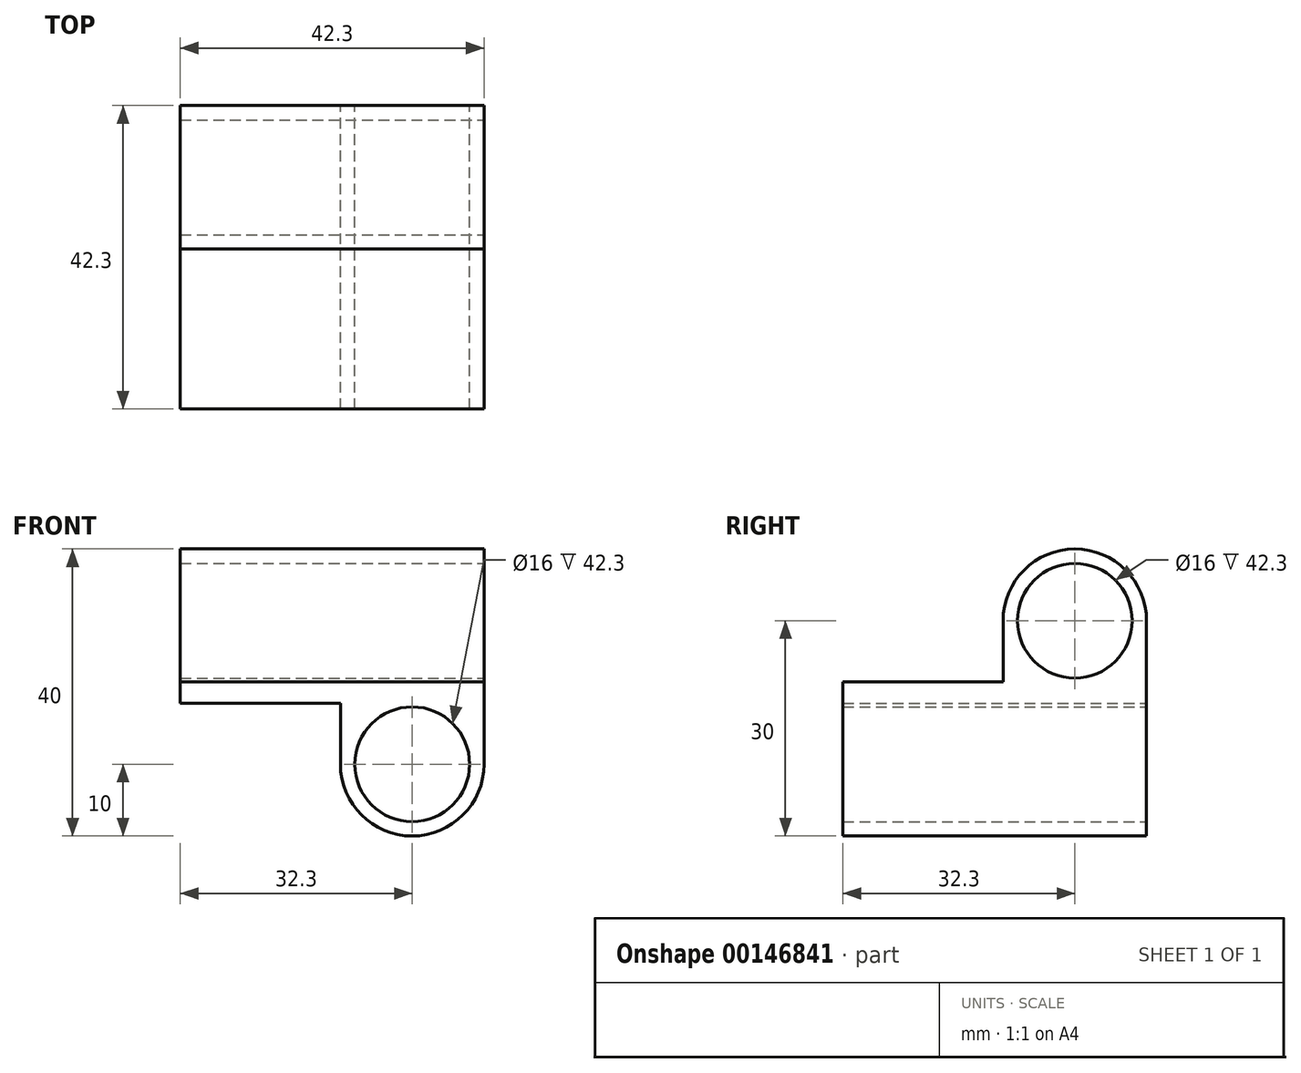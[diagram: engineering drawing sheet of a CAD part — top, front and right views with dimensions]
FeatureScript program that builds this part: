
annotation { "Feature Type Name" : "Feature", "Feature Type Description" : "" }
export const myFeature = defineFeature(function(context is Context, id is Id, definition is map)
    precondition{}
    {
        {
            var Q0;
            Q0=qCreatedBy(makeId("Front.planeOp"),FACE);
            var sketch = newSketch(context, id + "F0", { "sketchPlane" : qUnion([Q0])});
            skPoint(sketch, "E0.middle", {"position": v(0, 0) * mm});
            skCircle(sketch, "E1", {"center": v(-10, -10) * mm, "radius": 10 * mm});
            skCircle(sketch, "E2", {"center": v(-10, -10) * mm, "radius": 8 * mm});
            skLineSegment(sketch, "E3.bottom", {"start": v(0, 0) * mm, "end": v(-20, 0) * mm});
            skLineSegment(sketch, "E3.top", {"start": v(0, -10) * mm, "end": v(-20, -10) * mm});
            skLineSegment(sketch, "E3.left", {"start": v(0, 0) * mm, "end": v(0, -10) * mm});
            skLineSegment(sketch, "E3.right", {"start": v(-20, 0) * mm, "end": v(-20, -10) * mm});
            skLineSegment(sketch, "E4.bottom", {"start": v(-42.3, 0) * mm, "end": v(-20, 0) * mm});
            skLineSegment(sketch, "E4.top", {"start": v(-42.3, -1.5) * mm, "end": v(-20, -1.5) * mm});
            skLineSegment(sketch, "E4.left", {"start": v(-42.3, 0) * mm, "end": v(-42.3, -1.5) * mm});
            skLineSegment(sketch, "E4.right", {"start": v(-20, 0) * mm, "end": v(-20, -1.5) * mm});
            skSolve(sketch);
        }
        {
            var Q0;
            Q0=qSketchRegion(id+"F0",true);
            extrude(context, id + "F1", {"entities" : qUnion([Q0]), "depth" : 42.3 * mm});
        }
        {
            var Q0;
            Q0=qCreatedBy(makeId("Right.planeOp"),FACE);
            var sketch = newSketch(context, id + "F2", { "sketchPlane" : qUnion([Q0])});
            skCircle(sketch, "E5", {"center": v(-10, 10) * mm, "radius": 8 * mm});
            skCircle(sketch, "E6", {"center": v(-10, 10) * mm, "radius": 10 * mm});
            skPoint(sketch, "E7.middle", {"position": v(0, 0) * mm});
            skLineSegment(sketch, "E8.bottom", {"start": v(0, 0) * mm, "end": v(-20, 0) * mm});
            skLineSegment(sketch, "E8.top", {"start": v(0, 10) * mm, "end": v(-20, 10) * mm});
            skLineSegment(sketch, "E8.left", {"start": v(0, 0) * mm, "end": v(0, 10) * mm});
            skLineSegment(sketch, "E8.right", {"start": v(-20, 0) * mm, "end": v(-20, 10) * mm});
            skLineSegment(sketch, "E9.bottom", {"start": v(-42.3, 1.5) * mm, "end": v(-20, 1.5) * mm});
            skLineSegment(sketch, "E9.top", {"start": v(-42.3, 0) * mm, "end": v(-20, 0) * mm});
            skLineSegment(sketch, "E9.left", {"start": v(-42.3, 1.5) * mm, "end": v(-42.3, 0) * mm});
            skLineSegment(sketch, "E9.right", {"start": v(-20, 1.5) * mm, "end": v(-20, 0) * mm});
            skSolve(sketch);
        }
        {
            var Q0;
            Q0=qSketchRegion(id+"F2",true);
            extrude(context, id + "F3", {"entities" : qUnion([Q0]), "operationType" : NewBodyOperationType.ADD, "oppositeDirection" : true, "depth" : 42.3 * mm});
        }
    });
